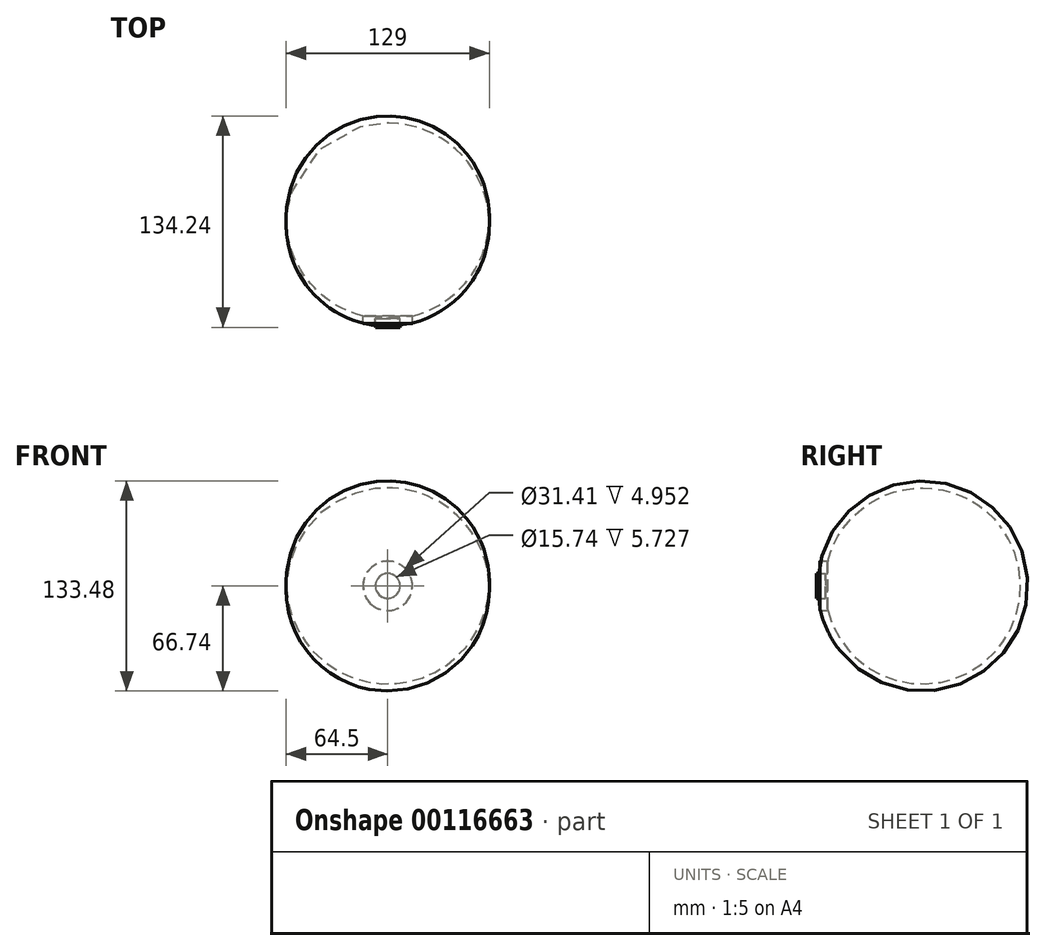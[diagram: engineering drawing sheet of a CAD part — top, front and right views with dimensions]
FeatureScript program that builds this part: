
annotation { "Feature Type Name" : "Feature", "Feature Type Description" : "" }
export const myFeature = defineFeature(function(context is Context, id is Id, definition is map)
    precondition{}
    {
        {
            var Q0;
            Q0=qCreatedBy(makeId("Front.planeOp"),FACE);
            var sketch = newSketch(context, id + "F0", { "sketchPlane" : qUnion([Q0])});
            skCircle(sketch, "E0", {"center": v(0, -2.23) * mm, "radius": 64.5 * mm});
            skLineSegment(sketch, "E1", {"start": v(-64.46, 0) * mm, "end": v(64.46, 0) * mm});
            skSolve(sketch);
        }
        {
            var Q0;
            {var subQ0=sQuery(id+"F0.wireOp",EDGE,"E1");Q0=makeQuery(id+"F0.imprint","IMPRINT",FACE,{"disambiguationData":[TD([[makeQuery(id+"F0.imprint","IMPRINT",EDGE,{"derivedFrom":subQ0}),1.0]])]});}
            var Q1;
            Q1=sQuery(id+"F0.wireOp",EDGE,"E1");
            revolve(context, id + "F1", {"entities" : qUnion([Q0]), "axis" : qUnion([Q1]), "revolveType" : RevolveType.FULL});
        }
        {
            var Q0;
            Q0=qCreatedBy(makeId("Front.planeOp"),FACE);
            var sketch = newSketch(context, id + "F2", { "sketchPlane" : qUnion([Q0])});
            skCircle(sketch, "E2", {"center": v(0, 0) * mm, "radius": 15.7 * mm});
            skCircle(sketch, "E3", {"center": v(0, 0) * mm, "radius": 7.92 * mm});
            skSolve(sketch);
        }
        {
            var Q0;
            Q0 = qSketchRegion(id + "F2", true);
            extrude(context, id + "F3", {"entities" : qUnion([Q0]), "operationType" : NewBodyOperationType.ADD, "depth" : 65.2 * mm});
        }
        {
            var Q0;
            Q0=qCreatedBy(makeId("Front.planeOp"),FACE);
            var sketch = newSketch(context, id + "F4", { "sketchPlane" : qUnion([Q0])});
            skCircle(sketch, "E4", {"center": v(0, 0) * mm, "radius": 7.87 * mm});
            skSolve(sketch);
        }
        {
            var Q0;
            Q0 = qSketchRegion(id + "F4", true);
            extrude(context, id + "F5", {"entities" : qUnion([Q0]), "operationType" : NewBodyOperationType.ADD, "depth" : 67.5 * mm});
        }
    });
